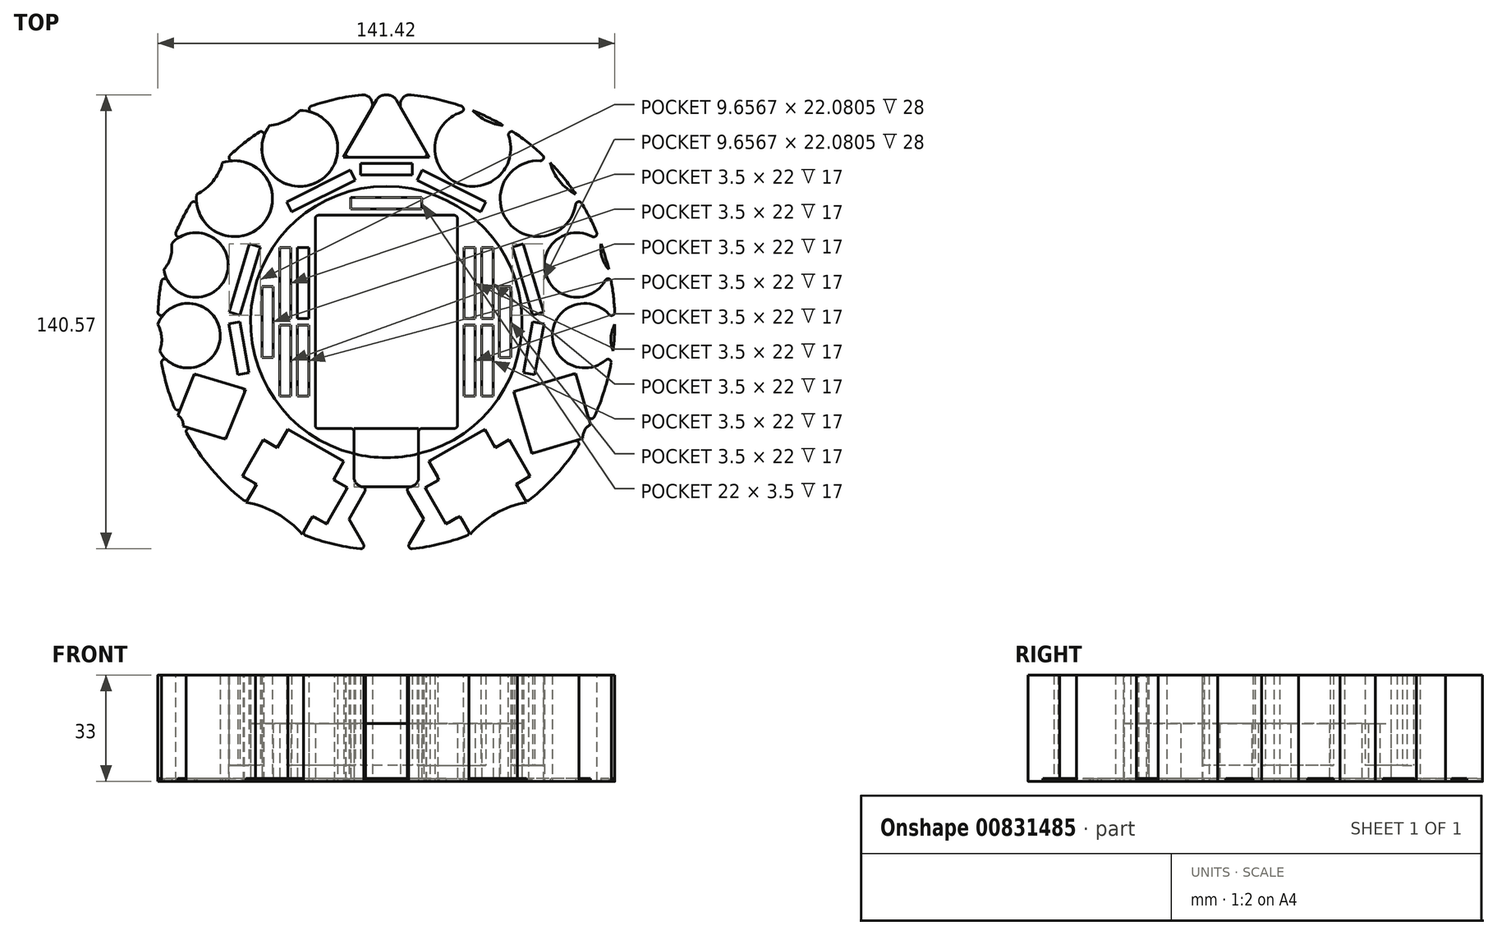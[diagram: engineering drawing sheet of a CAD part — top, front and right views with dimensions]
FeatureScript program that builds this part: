
annotation { "Feature Type Name" : "Feature", "Feature Type Description" : "" }
export const myFeature = defineFeature(function(context is Context, id is Id, definition is map)
    precondition{}
    {
        {
            var Q0;
            Q0=qCreatedBy(makeId("Top.planeOp"),FACE);
            var sketch = newSketch(context, id + "F0", { "sketchPlane" : qUnion([Q0])});
            skLineSegment(sketch, "E0.bottom", {"start": v(-22, 33) * mm, "end": v(22, 33) * mm});
            skLineSegment(sketch, "E0.top", {"start": v(-22, -33) * mm, "end": v(22, -33) * mm});
            skLineSegment(sketch, "E0.left", {"start": v(-22, 33) * mm, "end": v(-22, -33) * mm});
            skLineSegment(sketch, "E0.right", {"start": v(22, 33) * mm, "end": v(22, -33) * mm});
            skPoint(sketch, "E0.middle", {"position": v(0, 0) * mm});
            skCircle(sketch, "E1", {"center": v(0, 0) * mm, "radius": 42 * mm});
            skCircle(sketch, "E2", {"center": v(0, 0) * mm, "radius": 70.71 * mm});
            skPoint(sketch, "E3.middle", {"position": v(0, 57) * mm});
            skLineSegment(sketch, "E4.bottom", {"start": v(-10, -33) * mm, "end": v(10, -33) * mm});
            skLineSegment(sketch, "E4.top", {"start": v(-10, -51) * mm, "end": v(10, -51) * mm});
            skLineSegment(sketch, "E4.left", {"start": v(-10, -33) * mm, "end": v(-10, -51) * mm});
            skLineSegment(sketch, "E4.right", {"start": v(10, -33) * mm, "end": v(10, -51) * mm});
            skPoint(sketch, "E4.middle", {"position": v(0, -42) * mm});
            skCircle(sketch, "E5", {"center": v(0, 0) * mm, "radius": 60 * mm, "construction": true});
            skCircle(sketch, "E6", {"center": v(26.76, 53.7) * mm, "radius": 11.75 * mm});
            skCircle(sketch, "E7", {"center": v(0, 0) * mm, "radius": 61.5 * mm, "construction": true});
            skCircle(sketch, "E8", {"center": v(58.92, 17.62) * mm, "radius": 10 * mm});
            skCircle(sketch, "E9", {"center": v(0, 0) * mm, "radius": 60.5 * mm, "construction": true});
            skCircle(sketch, "E10", {"center": v(46.96, 38.14) * mm, "radius": 11.75 * mm});
            skCircle(sketch, "E11", {"center": v(61.35, -4.24) * mm, "radius": 10 * mm});
            skLineSegment(sketch, "E12", {"start": v(-13.28, 51) * mm, "end": v(13.28, 51) * mm});
            skLineSegment(sketch, "E13", {"start": v(13.28, 51) * mm, "end": v(0, 74) * mm});
            skLineSegment(sketch, "E14", {"start": v(0, 74) * mm, "end": v(-13.28, 51) * mm});
            skCircle(sketch, "E15", {"center": v(0, 0) * mm, "radius": 74 * mm, "construction": true});
            skCircle(sketch, "E16", {"center": v(0, 0) * mm, "radius": 59 * mm, "construction": true});
            skLineSegment(sketch, "E17", {"start": v(0, 0) * mm, "end": v(51.76, -28.32) * mm, "construction": true});
            skLineSegment(sketch, "E18.bottom", {"start": v(64.17, -35.1) * mm, "end": v(44.97, -40.72) * mm});
            skLineSegment(sketch, "E18.top", {"start": v(58.55, -15.91) * mm, "end": v(39.35, -21.53) * mm});
            skLineSegment(sketch, "E18.left", {"start": v(64.17, -35.1) * mm, "end": v(58.55, -15.91) * mm});
            skLineSegment(sketch, "E18.right", {"start": v(44.97, -40.72) * mm, "end": v(39.35, -21.53) * mm});
            skPoint(sketch, "E18.middle", {"position": v(51.76, -28.32) * mm});
            skCircle(sketch, "E19.MirrorC", {"center": v(-26.76, 53.7) * mm, "radius": 11.75 * mm});
            skCircle(sketch, "E20.MirrorC", {"center": v(-46.96, 38.14) * mm, "radius": 11.75 * mm});
            skCircle(sketch, "E21.MirrorC", {"center": v(-58.92, 17.62) * mm, "radius": 10 * mm});
            skCircle(sketch, "E22.MirrorC", {"center": v(-61.35, -4.24) * mm, "radius": 10 * mm});
            skLineSegment(sketch, "E23", {"start": v(-65.56, -31.45) * mm, "end": v(-49.7, -36.26) * mm});
            skLineSegment(sketch, "E24", {"start": v(-49.7, -36.26) * mm, "end": v(-43.54, -20.89) * mm});
            skLineSegment(sketch, "E25", {"start": v(-43.54, -20.89) * mm, "end": v(-59.39, -16.08) * mm});
            skLineSegment(sketch, "E26", {"start": v(-59.39, -16.08) * mm, "end": v(-65.56, -31.45) * mm});
            skLineSegment(sketch, "E27.bottom", {"start": v(-18.44, -62.59) * mm, "end": v(-44.5, -47.72) * mm});
            skLineSegment(sketch, "E27.top", {"start": v(-12, -51.3) * mm, "end": v(-38.06, -36.43) * mm});
            skLineSegment(sketch, "E27.left", {"start": v(-18.44, -62.59) * mm, "end": v(-12, -51.3) * mm});
            skLineSegment(sketch, "E27.right", {"start": v(-44.5, -47.72) * mm, "end": v(-38.06, -36.43) * mm});
            skPoint(sketch, "E27.middle", {"position": v(-28.25, -49.5) * mm});
            skLineSegment(sketch, "E28.bottom", {"start": v(-13.12, -43.17) * mm, "end": v(-30.5, -33.26) * mm});
            skLineSegment(sketch, "E28.top", {"start": v(-26, -65.75) * mm, "end": v(-43.38, -55.84) * mm});
            skLineSegment(sketch, "E28.left", {"start": v(-13.12, -43.17) * mm, "end": v(-26, -65.75) * mm});
            skLineSegment(sketch, "E28.right", {"start": v(-30.5, -33.26) * mm, "end": v(-43.38, -55.84) * mm});
            skLineSegment(sketch, "E29", {"start": v(0, 0) * mm, "end": v(-116.4, -55.84) * mm, "construction": true});
            skLineSegment(sketch, "E30.MirrorCS", {"start": v(13.12, -43.17) * mm, "end": v(30.5, -33.26) * mm});
            skLineSegment(sketch, "E31.MirrorCS", {"start": v(12, -51.3) * mm, "end": v(38.06, -36.43) * mm});
            skLineSegment(sketch, "E32.MirrorCS", {"start": v(30.5, -33.26) * mm, "end": v(43.38, -55.84) * mm});
            skLineSegment(sketch, "E33.MirrorCS", {"start": v(44.5, -47.72) * mm, "end": v(38.06, -36.43) * mm});
            skLineSegment(sketch, "E34.MirrorCS", {"start": v(18.44, -62.59) * mm, "end": v(12, -51.3) * mm});
            skLineSegment(sketch, "E35.MirrorCS", {"start": v(13.12, -43.17) * mm, "end": v(26, -65.75) * mm});
            skLineSegment(sketch, "E36.MirrorCS", {"start": v(26, -65.75) * mm, "end": v(43.38, -55.84) * mm});
            skLineSegment(sketch, "E37.MirrorCS", {"start": v(18.44, -62.59) * mm, "end": v(44.5, -47.72) * mm});
            skLineSegment(sketch, "E38", {"start": v(-24, 29.08) * mm, "end": v(-24, -29.92) * mm, "construction": true});
            skCircle(sketch, "E39", {"center": v(0, 0) * mm, "radius": 40 * mm, "construction": true});
            skLineSegment(sketch, "E40", {"start": v(-46.76, 1) * mm, "end": v(-10.29, 1) * mm, "construction": true});
            skLineSegment(sketch, "E41.bottom", {"start": v(-24, 1) * mm, "end": v(-27.5, 1) * mm});
            skLineSegment(sketch, "E41.top", {"start": v(-24, 23) * mm, "end": v(-27.5, 23) * mm});
            skLineSegment(sketch, "E41.left", {"start": v(-24, 1) * mm, "end": v(-24, 23) * mm});
            skLineSegment(sketch, "E41.right", {"start": v(-27.5, 1) * mm, "end": v(-27.5, 23) * mm});
            skLineSegment(sketch, "E42.bottom", {"start": v(-29.5, 1) * mm, "end": v(-33, 1) * mm});
            skLineSegment(sketch, "E42.top", {"start": v(-29.5, 23) * mm, "end": v(-33, 23) * mm});
            skLineSegment(sketch, "E42.left", {"start": v(-29.5, 1) * mm, "end": v(-29.5, 23) * mm});
            skLineSegment(sketch, "E42.right", {"start": v(-33, 1) * mm, "end": v(-33, 23) * mm});
            skLineSegment(sketch, "E43.bottom", {"start": v(-35, 11) * mm, "end": v(-38.5, 11) * mm});
            skLineSegment(sketch, "E43.top", {"start": v(-35, -11) * mm, "end": v(-38.5, -11) * mm});
            skLineSegment(sketch, "E43.left", {"start": v(-35, 11) * mm, "end": v(-35, -11) * mm});
            skLineSegment(sketch, "E43.right", {"start": v(-38.5, 11) * mm, "end": v(-38.5, -11) * mm});
            skPoint(sketch, "E43.middle", {"position": v(-36.75, 0) * mm});
            skLineSegment(sketch, "E44.MirrorCS", {"start": v(-29.5, -1) * mm, "end": v(-29.5, -23) * mm});
            skLineSegment(sketch, "E45.MirrorCS", {"start": v(-27.5, -1) * mm, "end": v(-27.5, -23) * mm});
            skLineSegment(sketch, "E46.MirrorCS", {"start": v(-29.5, -1) * mm, "end": v(-33, -1) * mm});
            skLineSegment(sketch, "E47.MirrorCS", {"start": v(-24, -1) * mm, "end": v(-27.5, -1) * mm});
            skLineSegment(sketch, "E48.MirrorCS", {"start": v(-24, -23) * mm, "end": v(-27.5, -23) * mm});
            skLineSegment(sketch, "E49.MirrorCS", {"start": v(-29.5, -23) * mm, "end": v(-33, -23) * mm});
            skLineSegment(sketch, "E50.MirrorCS", {"start": v(-33, -1) * mm, "end": v(-33, -23) * mm});
            skLineSegment(sketch, "E51.MirrorCS", {"start": v(-24, -1) * mm, "end": v(-24, -23) * mm});
            skLineSegment(sketch, "E52.MirrorCS", {"start": v(24, -1) * mm, "end": v(24, -23) * mm});
            skLineSegment(sketch, "E53.MirrorCS", {"start": v(24, 1) * mm, "end": v(24, 23) * mm});
            skLineSegment(sketch, "E54.MirrorCS", {"start": v(29.5, 1) * mm, "end": v(33, 1) * mm});
            skLineSegment(sketch, "E55.MirrorCS", {"start": v(29.5, -1) * mm, "end": v(33, -1) * mm});
            skLineSegment(sketch, "E56.MirrorCS", {"start": v(24, 1) * mm, "end": v(27.5, 1) * mm});
            skLineSegment(sketch, "E57.MirrorCS", {"start": v(24, -1) * mm, "end": v(27.5, -1) * mm});
            skLineSegment(sketch, "E58.MirrorCS", {"start": v(24, 29.08) * mm, "end": v(24, -29.92) * mm, "construction": true});
            skLineSegment(sketch, "E59.MirrorCS", {"start": v(24, -23) * mm, "end": v(27.5, -23) * mm});
            skLineSegment(sketch, "E60.MirrorCS", {"start": v(35, 11) * mm, "end": v(38.5, 11) * mm});
            skLineSegment(sketch, "E61.MirrorCS", {"start": v(29.5, -1) * mm, "end": v(29.5, -23) * mm});
            skLineSegment(sketch, "E62.MirrorCS", {"start": v(35, -11) * mm, "end": v(38.5, -11) * mm});
            skLineSegment(sketch, "E63.MirrorCS", {"start": v(29.5, 23) * mm, "end": v(33, 23) * mm});
            skLineSegment(sketch, "E64.MirrorCS", {"start": v(38.5, 11) * mm, "end": v(38.5, -11) * mm});
            skLineSegment(sketch, "E65.MirrorCS", {"start": v(24, 23) * mm, "end": v(27.5, 23) * mm});
            skPoint(sketch, "E66.MirrorP", {"position": v(36.75, 0) * mm});
            skLineSegment(sketch, "E67.MirrorCS", {"start": v(46.76, 1) * mm, "end": v(10.29, 1) * mm, "construction": true});
            skLineSegment(sketch, "E68.MirrorCS", {"start": v(27.5, -1) * mm, "end": v(27.5, -23) * mm});
            skLineSegment(sketch, "E69.MirrorCS", {"start": v(33, 1) * mm, "end": v(33, 23) * mm});
            skLineSegment(sketch, "E70.MirrorCS", {"start": v(35, 11) * mm, "end": v(35, -11) * mm});
            skLineSegment(sketch, "E71.MirrorCS", {"start": v(29.5, -23) * mm, "end": v(33, -23) * mm});
            skLineSegment(sketch, "E72.MirrorCS", {"start": v(29.5, 1) * mm, "end": v(29.5, 23) * mm});
            skLineSegment(sketch, "E73.MirrorCS", {"start": v(27.5, 1) * mm, "end": v(27.5, 23) * mm});
            skLineSegment(sketch, "E74.MirrorCS", {"start": v(33, -1) * mm, "end": v(33, -23) * mm});
            skLineSegment(sketch, "E75.bottom", {"start": v(11, 35) * mm, "end": v(-11, 35) * mm});
            skLineSegment(sketch, "E75.top", {"start": v(11, 38.5) * mm, "end": v(-11, 38.5) * mm});
            skLineSegment(sketch, "E75.left", {"start": v(11, 35) * mm, "end": v(11, 38.5) * mm});
            skLineSegment(sketch, "E75.right", {"start": v(-11, 35) * mm, "end": v(-11, 38.5) * mm});
            skPoint(sketch, "E75.middle", {"position": v(0, 36.75) * mm});
            skLineSegment(sketch, "E76", {"start": v(0, 0) * mm, "end": v(-26.76, 53.7) * mm, "construction": true});
            skLineSegment(sketch, "E77.bottom", {"start": v(-11.12, 46.97) * mm, "end": v(-30.8, 37.16) * mm});
            skLineSegment(sketch, "E77.top", {"start": v(-9.56, 43.84) * mm, "end": v(-29.25, 34.03) * mm});
            skLineSegment(sketch, "E77.left", {"start": v(-11.12, 46.97) * mm, "end": v(-9.56, 43.84) * mm});
            skLineSegment(sketch, "E77.right", {"start": v(-30.8, 37.16) * mm, "end": v(-29.25, 34.03) * mm});
            skPoint(sketch, "E77.middle", {"position": v(-20.18, 40.5) * mm});
            skLineSegment(sketch, "E78", {"start": v(-58.92, 17.62) * mm, "end": v(0, 0) * mm, "construction": true});
            skLineSegment(sketch, "E79.bottom", {"start": v(-39, 23.15) * mm, "end": v(-42.36, 24.15) * mm});
            skLineSegment(sketch, "E79.top", {"start": v(-45.3, 2.07) * mm, "end": v(-48.66, 3.07) * mm});
            skLineSegment(sketch, "E79.left", {"start": v(-39, 23.15) * mm, "end": v(-45.3, 2.07) * mm});
            skLineSegment(sketch, "E79.right", {"start": v(-42.36, 24.15) * mm, "end": v(-48.66, 3.07) * mm});
            skPoint(sketch, "E79.middle", {"position": v(-43.83, 13.1) * mm});
            skLineSegment(sketch, "E80.MirrorCS", {"start": v(30.8, 37.16) * mm, "end": v(29.25, 34.03) * mm});
            skLineSegment(sketch, "E81.MirrorCS", {"start": v(11.12, 46.97) * mm, "end": v(30.8, 37.16) * mm});
            skLineSegment(sketch, "E82.MirrorCS", {"start": v(9.56, 43.84) * mm, "end": v(29.25, 34.03) * mm});
            skLineSegment(sketch, "E83.MirrorCS", {"start": v(11.12, 46.97) * mm, "end": v(9.56, 43.84) * mm});
            skLineSegment(sketch, "E84.MirrorCS", {"start": v(42.36, 24.15) * mm, "end": v(48.66, 3.07) * mm});
            skLineSegment(sketch, "E85.MirrorCS", {"start": v(39, 23.15) * mm, "end": v(45.3, 2.07) * mm});
            skLineSegment(sketch, "E86.MirrorCS", {"start": v(39, 23.15) * mm, "end": v(42.36, 24.15) * mm});
            skLineSegment(sketch, "E87.MirrorCS", {"start": v(45.3, 2.07) * mm, "end": v(48.66, 3.07) * mm});
            skLineSegment(sketch, "E88.bottom", {"start": v(8, 45.5) * mm, "end": v(-8, 45.5) * mm});
            skLineSegment(sketch, "E88.top", {"start": v(8, 49) * mm, "end": v(-8, 49) * mm});
            skLineSegment(sketch, "E88.left", {"start": v(8, 45.5) * mm, "end": v(8, 49) * mm});
            skLineSegment(sketch, "E88.right", {"start": v(-8, 45.5) * mm, "end": v(-8, 49) * mm});
            skPoint(sketch, "E88.middle", {"position": v(0, 47.25) * mm});
            skLineSegment(sketch, "E89", {"start": v(0, 0) * mm, "end": v(-52.56, -9.43) * mm, "construction": true});
            skLineSegment(sketch, "E90.bottom", {"start": v(-48.75, -0.62) * mm, "end": v(-45.3, 0) * mm});
            skLineSegment(sketch, "E90.top", {"start": v(-45.93, -16.37) * mm, "end": v(-42.48, -15.75) * mm});
            skLineSegment(sketch, "E90.left", {"start": v(-48.75, -0.62) * mm, "end": v(-45.93, -16.37) * mm});
            skLineSegment(sketch, "E90.right", {"start": v(-45.3, 0) * mm, "end": v(-42.48, -15.75) * mm});
            skPoint(sketch, "E90.middle", {"position": v(-45.62, -8.18) * mm});
            skLineSegment(sketch, "E91.MirrorCS", {"start": v(48.75, -0.62) * mm, "end": v(45.3, 0) * mm});
            skLineSegment(sketch, "E92.MirrorCS", {"start": v(45.93, -16.37) * mm, "end": v(42.48, -15.75) * mm});
            skLineSegment(sketch, "E93.MirrorCS", {"start": v(48.75, -0.62) * mm, "end": v(45.93, -16.37) * mm});
            skLineSegment(sketch, "E94.MirrorCS", {"start": v(45.3, 0) * mm, "end": v(42.48, -15.75) * mm});
            skPoint(sketch, "E95.MirrorP", {"position": v(45.62, -8.18) * mm});
            skLineSegment(sketch, "E96", {"start": v(-45.3, 2.07) * mm, "end": v(-45.3, -7.96) * mm, "construction": true});
            skCircle(sketch, "E97.cCircle", {"center": v(0, -61) * mm, "radius": 10 * mm, "construction": true});
            skLineSegment(sketch, "E97.0", {"start": v(-5.77, -51) * mm, "end": v(5.77, -51) * mm});
            skLineSegment(sketch, "E97.1", {"start": v(5.77, -51) * mm, "end": v(11.55, -61) * mm});
            skLineSegment(sketch, "E97.2", {"start": v(11.55, -61) * mm, "end": v(5.77, -71) * mm});
            skLineSegment(sketch, "E97.3", {"start": v(5.77, -71) * mm, "end": v(-5.77, -71) * mm});
            skLineSegment(sketch, "E97.4", {"start": v(-5.77, -71) * mm, "end": v(-11.55, -61) * mm});
            skLineSegment(sketch, "E97.5", {"start": v(-11.55, -61) * mm, "end": v(-5.77, -51) * mm});
            skPoint(sketch, "E97.0.midPoint", {"position": v(0, -51) * mm});
            skArc(sketch, "E98", {"start": v(-26, -65.75) * mm, "mid": v(-33.84, -59.3) * mm, "end": v(-43.38, -55.84) * mm});
            skArc(sketch, "E99", {"start": v(43.38, -55.84) * mm, "mid": v(33.84, -59.3) * mm, "end": v(26, -65.75) * mm});
            skArc(sketch, "E100", {"start": v(6.1, -70.45) * mm, "mid": v(0, -69.82) * mm, "end": v(-6.1, -70.45) * mm});
            skArc(sketch, "E101", {"start": v(-62.93, -32.25) * mm, "mid": v(-63.18, -30.31) * mm, "end": v(-64.53, -28.9) * mm});
            skArc(sketch, "E102", {"start": v(-70.13, -9.03) * mm, "mid": v(-69.5, -4.8) * mm, "end": v(-70.7, -0.7) * mm});
            skArc(sketch, "E103", {"start": v(-68.82, 16.23) * mm, "mid": v(-66.75, 19.96) * mm, "end": v(-66.43, 24.22) * mm});
            skArc(sketch, "E104", {"start": v(-58.63, 39.53) * mm, "mid": v(-53.6, 43.53) * mm, "end": v(-50.71, 49.28) * mm});
            skArc(sketch, "E105", {"start": v(-36.14, 60.78) * mm, "mid": v(-31.03, 62.27) * mm, "end": v(-26.76, 65.45) * mm});
            skArc(sketch, "E106", {"start": v(-1.91, 70.68) * mm, "mid": v(0, 70.2) * mm, "end": v(1.91, 70.68) * mm});
            skArc(sketch, "E107", {"start": v(63.18, -31.75) * mm, "mid": v(61.34, -33.56) * mm, "end": v(60.8, -36.09) * mm});
            skArc(sketch, "E108.MirrorCS", {"start": v(36.14, 60.78) * mm, "mid": v(31.03, 62.27) * mm, "end": v(26.76, 65.45) * mm});
            skArc(sketch, "E109.MirrorCS", {"start": v(58.63, 39.53) * mm, "mid": v(53.6, 43.53) * mm, "end": v(50.71, 49.28) * mm});
            skArc(sketch, "E110.MirrorCS", {"start": v(68.82, 16.23) * mm, "mid": v(66.75, 19.96) * mm, "end": v(66.43, 24.22) * mm});
            skArc(sketch, "E111.MirrorCS", {"start": v(70.13, -9.03) * mm, "mid": v(69.5, -4.8) * mm, "end": v(70.7, -0.7) * mm});
            skSolve(sketch);
        }
        {
            var Q0;
            Q0=makeQuery(id+"F0.imprint","IMPRINT",FACE,{"disambiguationData":[TD([[makeQuery(id+"F0.imprint","IMPRINT",EDGE,{"derivedFrom":sQuery(id+"F0.wireOp",EDGE,"E0.bottom")}),1.0]])]});
            extrude(context, id + "F1", {"entities" : qUnion([Q0]), "depth" : 18 * mm, "offsetDistance" : 25 * mm});
        }
        {
            var Q0;
            {var subQ0=sQuery(id+"F0.wireOp",EDGE,"E3.bottom");Q0=makeQuery(id+"F0.imprint","IMPRINT",FACE,{"disambiguationData":[TD([[makeQuery(id+"F0.imprint","IMPRINT",EDGE,{"derivedFrom":subQ0}),-1.0]])]});}
            var Q1;
            {var subQ0=sQuery(id+"F0.wireOp",EDGE,"wK9GQTOU-0l9T-mlqG-xWPM-1yL7ZsGGjNM9.top");var subQ1=sQuery(id+"F0.wireOp",EDGE,"E3.left");var subQ2=makeQuery(id+"F0.imprint","INTERSECT",VERTEX,{"derivedFrom":[subQ1,subQ0]});Q1=makeQuery(id+"F0.imprint","IMPRINT",FACE,{"disambiguationData":[TD([[makeQuery(id+"F0.imprint","IMPRINT",EDGE,{"disambiguationData":[TD([[subQ2,-1.0]])],"derivedFrom":subQ1}),1.0]])]});}
            var Q2;
            {var subQ5=sQuery(id+"F0.wireOp",EDGE,"wK9GQTOU-0l9T-mlqG-xWPM-1yL7ZsGGjNM9.right");Q2=makeQuery(id+"F0.imprint","IMPRINT",FACE,{"disambiguationData":[TD([[makeQuery(id+"F0.imprint","IMPRINT",EDGE,{"derivedFrom":subQ5}),-1.0]])]});}
            var Q3;
            {var subQ5=sQuery(id+"F0.wireOp",EDGE,"wK9GQTOU-0l9T-mlqG-xWPM-1yL7ZsGGjNM9.left");Q3=makeQuery(id+"F0.imprint","IMPRINT",FACE,{"disambiguationData":[TD([[makeQuery(id+"F0.imprint","IMPRINT",EDGE,{"derivedFrom":subQ5}),1.0]])]});}
            var Q4;
            {var subQ0=sQuery(id+"F0.wireOp",EDGE,"E3.top");Q4=makeQuery(id+"F0.imprint","IMPRINT",FACE,{"disambiguationData":[TD([[makeQuery(id+"F0.imprint","IMPRINT",EDGE,{"derivedFrom":subQ0}),1.0]])]});}
            var Q5;
            {var subQ0=sQuery(id+"F0.wireOp",EDGE,"E3.bottom");Q5=makeQuery(id+"F0.imprint","IMPRINT",FACE,{"disambiguationData":[TD([[makeQuery(id+"F0.imprint","IMPRINT",EDGE,{"derivedFrom":subQ0}),1.0]])]});}
            var Q6;
            Q6=makeQuery(id+"F0.imprint","IMPRINT",FACE,{"disambiguationData":[TD([[makeQuery(id+"F0.imprint","IMPRINT",EDGE,{"derivedFrom":sQuery(id+"F0.wireOp",EDGE,"E0.bottom")}),-1.0]])]});
            var Q7;
            {var subQ5=sQuery(id+"F0.wireOp",EDGE,"E4.top");Q7=makeQuery(id+"F0.imprint","IMPRINT",FACE,{"disambiguationData":[TD([[makeQuery(id+"F0.imprint","IMPRINT",EDGE,{"derivedFrom":subQ5}),1.0]])]});}
            var Q8;
            {var subQ5=sQuery(id+"F0.wireOp",EDGE,"E4.bottom");Q8=makeQuery(id+"F0.imprint","IMPRINT",FACE,{"disambiguationData":[TD([[makeQuery(id+"F0.imprint","IMPRINT",EDGE,{"derivedFrom":subQ5}),-1.0]])]});}
            var Q9;
            {var subQ0=sQuery(id+"F0.wireOp",EDGE,"382944a8-2fda-4f8f-b6c7-34ecd0944c6e0.MirrorCS");Q9=makeQuery(id+"F0.imprint","IMPRINT",FACE,{"disambiguationData":[TD([[makeQuery(id+"F0.imprint","IMPRINT",EDGE,{"derivedFrom":subQ0}),-1.0]])]});}
            var Q10;
            {var subQ0=sQuery(id+"F0.wireOp",EDGE,"E18.top");Q10=makeQuery(id+"F0.imprint","IMPRINT",FACE,{"disambiguationData":[TD([[makeQuery(id+"F0.imprint","IMPRINT",EDGE,{"derivedFrom":subQ0}),1.0]])]});}
            var Q11;
            {var subQ1=sQuery(id+"F0.wireOp",EDGE,"E24");Q11=makeQuery(id+"F0.imprint","IMPRINT",FACE,{"disambiguationData":[TD([[makeQuery(id+"F0.imprint","IMPRINT",EDGE,{"derivedFrom":subQ1}),1.0]])]});}
            var Q12;
            {var subQ5=sQuery(id+"F0.wireOp",EDGE,"E12");Q12=makeQuery(id+"F0.imprint","IMPRINT",FACE,{"disambiguationData":[TD([[makeQuery(id+"F0.imprint","IMPRINT",EDGE,{"derivedFrom":subQ5}),1.0]])]});}
            var Q13;
            {var subQ5=sQuery(id+"F0.wireOp",EDGE,"E28.bottom");Q13=makeQuery(id+"F0.imprint","IMPRINT",FACE,{"disambiguationData":[TD([[makeQuery(id+"F0.imprint","IMPRINT",EDGE,{"derivedFrom":subQ5}),1.0]])]});}
            var Q14;
            {var subQ0=sQuery(id+"F0.wireOp",EDGE,"E27.right");Q14=makeQuery(id+"F0.imprint","IMPRINT",FACE,{"disambiguationData":[TD([[makeQuery(id+"F0.imprint","IMPRINT",EDGE,{"derivedFrom":subQ0}),-1.0]])]});}
            var Q15;
            {var subQ0=sQuery(id+"F0.wireOp",EDGE,"E28.left");var subQ1=sQuery(id+"F0.wireOp",EDGE,"E27.bottom");var subQ2=makeQuery(id+"F0.imprint","INTERSECT",VERTEX,{"derivedFrom":[subQ1,subQ0]});Q15=makeQuery(id+"F0.imprint","IMPRINT",FACE,{"disambiguationData":[TD([[makeQuery(id+"F0.imprint","IMPRINT",EDGE,{"disambiguationData":[TD([[subQ2,-1.0]])],"derivedFrom":subQ1}),-1.0]])]});}
            var Q16;
            {var subQ0=sQuery(id+"F0.wireOp",EDGE,"E27.left");Q16=makeQuery(id+"F0.imprint","IMPRINT",FACE,{"disambiguationData":[TD([[makeQuery(id+"F0.imprint","IMPRINT",EDGE,{"derivedFrom":subQ0}),1.0]])]});}
            var Q17;
            {var subQ0=sQuery(id+"F0.wireOp",EDGE,"E30.MirrorCS");Q17=makeQuery(id+"F0.imprint","IMPRINT",FACE,{"disambiguationData":[TD([[makeQuery(id+"F0.imprint","IMPRINT",EDGE,{"derivedFrom":subQ0}),-1.0]])]});}
            var Q18;
            {var subQ0=sQuery(id+"F0.wireOp",EDGE,"E35.MirrorCS");var subQ1=sQuery(id+"F0.wireOp",EDGE,"E31.MirrorCS");var subQ2=makeQuery(id+"F0.imprint","INTERSECT",VERTEX,{"derivedFrom":[subQ1,subQ0]});Q18=makeQuery(id+"F0.imprint","IMPRINT",FACE,{"disambiguationData":[TD([[makeQuery(id+"F0.imprint","IMPRINT",EDGE,{"disambiguationData":[TD([[subQ2,-1.0]])],"derivedFrom":subQ1}),-1.0]])]});}
            var Q19;
            {var subQ0=sQuery(id+"F0.wireOp",EDGE,"E34.MirrorCS");Q19=makeQuery(id+"F0.imprint","IMPRINT",FACE,{"disambiguationData":[TD([[makeQuery(id+"F0.imprint","IMPRINT",EDGE,{"derivedFrom":subQ0}),-1.0]])]});}
            var Q20;
            {var subQ0=sQuery(id+"F0.wireOp",EDGE,"E33.MirrorCS");Q20=makeQuery(id+"F0.imprint","IMPRINT",FACE,{"disambiguationData":[TD([[makeQuery(id+"F0.imprint","IMPRINT",EDGE,{"derivedFrom":subQ0}),1.0]])]});}
            var Q21;
            Q21=makeQuery(id+"F0.imprint","IMPRINT",FACE,{"disambiguationData":[TD([[makeQuery(id+"F0.imprint","IMPRINT",EDGE,{"derivedFrom":sQuery(id+"F0.wireOp",EDGE,"E43.bottom")}),1.0]])]});
            var Q22;
            Q22=makeQuery(id+"F0.imprint","IMPRINT",FACE,{"disambiguationData":[TD([[makeQuery(id+"F0.imprint","IMPRINT",EDGE,{"derivedFrom":sQuery(id+"F0.wireOp",EDGE,"E42.bottom")}),-1.0]])]});
            var Q23;
            Q23=makeQuery(id+"F0.imprint","IMPRINT",FACE,{"disambiguationData":[TD([[makeQuery(id+"F0.imprint","IMPRINT",EDGE,{"derivedFrom":sQuery(id+"F0.wireOp",EDGE,"E41.bottom")}),-1.0]])]});
            var Q24;
            Q24=makeQuery(id+"F0.imprint","IMPRINT",FACE,{"disambiguationData":[TD([[makeQuery(id+"F0.imprint","IMPRINT",EDGE,{"derivedFrom":sQuery(id+"F0.wireOp",EDGE,"E44.MirrorCS")}),-1.0]])]});
            var Q25;
            Q25=makeQuery(id+"F0.imprint","IMPRINT",FACE,{"disambiguationData":[TD([[makeQuery(id+"F0.imprint","IMPRINT",EDGE,{"derivedFrom":sQuery(id+"F0.wireOp",EDGE,"E53.MirrorCS")}),-1.0]])]});
            var Q26;
            Q26=makeQuery(id+"F0.imprint","IMPRINT",FACE,{"disambiguationData":[TD([[makeQuery(id+"F0.imprint","IMPRINT",EDGE,{"derivedFrom":sQuery(id+"F0.wireOp",EDGE,"E54.MirrorCS")}),1.0]])]});
            var Q27;
            Q27=makeQuery(id+"F0.imprint","IMPRINT",FACE,{"disambiguationData":[TD([[makeQuery(id+"F0.imprint","IMPRINT",EDGE,{"derivedFrom":sQuery(id+"F0.wireOp",EDGE,"E60.MirrorCS")}),-1.0]])]});
            var Q28;
            Q28=makeQuery(id+"F0.imprint","IMPRINT",FACE,{"disambiguationData":[TD([[makeQuery(id+"F0.imprint","IMPRINT",EDGE,{"derivedFrom":sQuery(id+"F0.wireOp",EDGE,"E55.MirrorCS")}),-1.0]])]});
            var Q29;
            Q29=makeQuery(id+"F0.imprint","IMPRINT",FACE,{"disambiguationData":[TD([[makeQuery(id+"F0.imprint","IMPRINT",EDGE,{"derivedFrom":sQuery(id+"F0.wireOp",EDGE,"E52.MirrorCS")}),1.0]])]});
            var Q30;
            Q30=makeQuery(id+"F0.imprint","IMPRINT",FACE,{"disambiguationData":[TD([[makeQuery(id+"F0.imprint","IMPRINT",EDGE,{"derivedFrom":sQuery(id+"F0.wireOp",EDGE,"E45.MirrorCS")}),1.0]])]});
            var Q31;
            Q31=makeQuery(id+"F0.imprint","IMPRINT",FACE,{"disambiguationData":[TD([[makeQuery(id+"F0.imprint","IMPRINT",EDGE,{"derivedFrom":sQuery(id+"F0.wireOp",EDGE,"E75.bottom")}),-1.0]])]});
            var Q32;
            Q32=makeQuery(id+"F0.imprint","IMPRINT",FACE,{"disambiguationData":[TD([[makeQuery(id+"F0.imprint","IMPRINT",EDGE,{"derivedFrom":sQuery(id+"F0.wireOp",EDGE,"E97.0")}),-1.0]])]});
            var Q33;
            {var subQ5=sQuery(id+"F0.wireOp",EDGE,"E98");Q33=makeQuery(id+"F0.imprint","IMPRINT",FACE,{"disambiguationData":[TD([[makeQuery(id+"F0.imprint","IMPRINT",EDGE,{"derivedFrom":subQ5}),-1.0]])]});}
            var Q34;
            {var subQ0=sQuery(id+"F0.wireOp",EDGE,"E99");Q34=makeQuery(id+"F0.imprint","IMPRINT",FACE,{"disambiguationData":[TD([[makeQuery(id+"F0.imprint","IMPRINT",EDGE,{"derivedFrom":subQ0}),-1.0]])]});}
            var Q35;
            {var subQ0=sQuery(id+"F0.wireOp",EDGE,"E102");Q35=makeQuery(id+"F0.imprint","IMPRINT",FACE,{"disambiguationData":[TD([[makeQuery(id+"F0.imprint","IMPRINT",EDGE,{"derivedFrom":subQ0}),-1.0]])]});}
            var Q36;
            {var subQ0=sQuery(id+"F0.wireOp",EDGE,"E103");Q36=makeQuery(id+"F0.imprint","IMPRINT",FACE,{"disambiguationData":[TD([[makeQuery(id+"F0.imprint","IMPRINT",EDGE,{"derivedFrom":subQ0}),-1.0]])]});}
            var Q37;
            {var subQ0=sQuery(id+"F0.wireOp",EDGE,"E104");Q37=makeQuery(id+"F0.imprint","IMPRINT",FACE,{"disambiguationData":[TD([[makeQuery(id+"F0.imprint","IMPRINT",EDGE,{"derivedFrom":subQ0}),-1.0]])]});}
            var Q38;
            {var subQ0=sQuery(id+"F0.wireOp",EDGE,"E105");Q38=makeQuery(id+"F0.imprint","IMPRINT",FACE,{"disambiguationData":[TD([[makeQuery(id+"F0.imprint","IMPRINT",EDGE,{"derivedFrom":subQ0}),-1.0]])]});}
            var Q39;
            {var subQ0=sQuery(id+"F0.wireOp",EDGE,"E108.MirrorCS");Q39=makeQuery(id+"F0.imprint","IMPRINT",FACE,{"disambiguationData":[TD([[makeQuery(id+"F0.imprint","IMPRINT",EDGE,{"derivedFrom":subQ0}),1.0]])]});}
            var Q40;
            {var subQ0=sQuery(id+"F0.wireOp",EDGE,"E109.MirrorCS");Q40=makeQuery(id+"F0.imprint","IMPRINT",FACE,{"disambiguationData":[TD([[makeQuery(id+"F0.imprint","IMPRINT",EDGE,{"derivedFrom":subQ0}),1.0]])]});}
            var Q41;
            {var subQ0=sQuery(id+"F0.wireOp",EDGE,"E110.MirrorCS");Q41=makeQuery(id+"F0.imprint","IMPRINT",FACE,{"disambiguationData":[TD([[makeQuery(id+"F0.imprint","IMPRINT",EDGE,{"derivedFrom":subQ0}),1.0]])]});}
            var Q42;
            {var subQ0=sQuery(id+"F0.wireOp",EDGE,"E111.MirrorCS");Q42=makeQuery(id+"F0.imprint","IMPRINT",FACE,{"disambiguationData":[TD([[makeQuery(id+"F0.imprint","IMPRINT",EDGE,{"derivedFrom":subQ0}),1.0]])]});}
            extrude(context, id + "F2", {"entities" : qUnion([Q0, Q1, Q2, Q3, Q4, Q5, Q6, Q7, Q8, Q9, Q10, Q11, Q12, Q13, Q14, Q15, Q16, Q17, Q18, Q19, Q20, Q21, Q22, Q23, Q24, Q25, Q26, Q27, Q28, Q29, Q30, Q31, Q32, Q33, Q34, Q35, Q36, Q37, Q38, Q39, Q40, Q41, Q42]), "operationType" : NewBodyOperationType.ADD, "depth" : 1 * mm, "offsetDistance" : 25 * mm});
        }
        {
            var Q0;
            Q0=makeQuery(id+"F1.opExtrude","SWEPT_EDGE",EDGE,{"disambiguationData":[OSD([sQuery(id+"F0.wireOp",EDGE,"E0.bottom"),sQuery(id+"F0.wireOp",EDGE,"E0.left")])]});
            var Q1;
            Q1=makeQuery(id+"F1.opExtrude","SWEPT_EDGE",EDGE,{"disambiguationData":[OSD([sQuery(id+"F0.wireOp",EDGE,"E0.bottom"),sQuery(id+"F0.wireOp",EDGE,"E0.right")])]});
            var Q2;
            Q2=makeQuery(id+"F1.opExtrude","SWEPT_EDGE",EDGE,{"disambiguationData":[OSD([sQuery(id+"F0.wireOp",EDGE,"E0.top"),sQuery(id+"F0.wireOp",EDGE,"E0.left")])]});
            var Q3;
            Q3=makeQuery(id+"F1.opExtrude","SWEPT_EDGE",EDGE,{"disambiguationData":[OSD([sQuery(id+"F0.wireOp",EDGE,"E0.top"),sQuery(id+"F0.wireOp",EDGE,"E4.bottom"),sQuery(id+"F0.wireOp",EDGE,"E4.left")])]});
            var Q4;
            Q4=makeQuery(id+"F1.opExtrude","SWEPT_EDGE",EDGE,{"disambiguationData":[OSD([sQuery(id+"F0.wireOp",EDGE,"E0.top"),sQuery(id+"F0.wireOp",EDGE,"E4.bottom"),sQuery(id+"F0.wireOp",EDGE,"E4.right")])]});
            var Q5;
            Q5=makeQuery(id+"F1.opExtrude","SWEPT_EDGE",EDGE,{"disambiguationData":[OSD([sQuery(id+"F0.wireOp",EDGE,"E0.top"),sQuery(id+"F0.wireOp",EDGE,"E0.right")])]});
            fillet(context, id + "F3", {"entities" : qUnion([Q0, Q1, Q2, Q3, Q4, Q5]), "radius" : 1 * mm, "tangentPropagation" : true, "allowEdgeOverflow" : false});
        }
        {
            var Q0;
            {var subQ69=sQuery(id+"F0.wireOp",EDGE,"E4.top");Q0=makeQuery(id+"F0.imprint","IMPRINT",FACE,{"disambiguationData":[TD([[makeQuery(id+"F0.imprint","IMPRINT",EDGE,{"derivedFrom":subQ69}),-1.0]])]});}
            extrude(context, id + "F4", {"entities" : qUnion([Q0]), "depth" : 33 * mm, "offsetDistance" : 25 * mm});
        }
        {
            var Q0;
            Q0=makeQuery(id+"F4.opExtrude","SWEPT_EDGE",EDGE,{"disambiguationData":[OSD([sQuery(id+"F0.wireOp",EDGE,"E2"),sQuery(id+"F0.wireOp",EDGE,"E28.top"),sQuery(id+"F0.wireOp",EDGE,"E28.left")])]});
            var Q1;
            Q1=makeQuery(id+"F4.opExtrude","SWEPT_EDGE",EDGE,{"disambiguationData":[OSD([sQuery(id+"F0.wireOp",EDGE,"E2"),sQuery(id+"F0.wireOp",EDGE,"E28.top"),sQuery(id+"F0.wireOp",EDGE,"E28.right")])]});
            var Q2;
            Q2=makeQuery(id+"F4.opExtrude","SWEPT_EDGE",EDGE,{"disambiguationData":[OSD([sQuery(id+"F0.wireOp",EDGE,"E2"),sQuery(id+"F0.wireOp",EDGE,"E23")])]});
            var Q3;
            Q3=makeQuery(id+"F4.opExtrude","SWEPT_EDGE",EDGE,{"disambiguationData":[OSD([sQuery(id+"F0.wireOp",EDGE,"E2"),sQuery(id+"F0.wireOp",EDGE,"E26")])]});
            var Q4;
            {var subQ0=sQuery(id+"F0.wireOp",EDGE,"E22.MirrorC");var subQ1=sQuery(id+"F0.wireOp",EDGE,"E2");Q4=makeQuery(id+"F4.opExtrude","SWEPT_EDGE",EDGE,{"disambiguationData":[OSD([subQ1,subQ0]),TDD([makeQuery(id+"F0.imprint","INTERSECT",VERTEX,{"disambiguationData":[OD(1.0)],"derivedFrom":[subQ1,subQ0]})])]});}
            var Q5;
            {var subQ0=sQuery(id+"F0.wireOp",EDGE,"E22.MirrorC");var subQ1=sQuery(id+"F0.wireOp",EDGE,"E2");Q5=makeQuery(id+"F4.opExtrude","SWEPT_EDGE",EDGE,{"disambiguationData":[OSD([subQ1,subQ0]),TDD([makeQuery(id+"F0.imprint","INTERSECT",VERTEX,{"disambiguationData":[OD(0.0)],"derivedFrom":[subQ1,subQ0]})])]});}
            var Q6;
            {var subQ0=sQuery(id+"F0.wireOp",EDGE,"E21.MirrorC");var subQ1=sQuery(id+"F0.wireOp",EDGE,"E2");Q6=makeQuery(id+"F4.opExtrude","SWEPT_EDGE",EDGE,{"disambiguationData":[OSD([subQ1,subQ0]),TDD([makeQuery(id+"F0.imprint","INTERSECT",VERTEX,{"disambiguationData":[OD(0.0)],"derivedFrom":[subQ1,subQ0]})])]});}
            var Q7;
            {var subQ0=sQuery(id+"F0.wireOp",EDGE,"E20.MirrorC");var subQ1=sQuery(id+"F0.wireOp",EDGE,"E2");Q7=makeQuery(id+"F4.opExtrude","SWEPT_EDGE",EDGE,{"disambiguationData":[OSD([subQ1,subQ0]),TDD([makeQuery(id+"F0.imprint","INTERSECT",VERTEX,{"disambiguationData":[OD(1.0)],"derivedFrom":[subQ1,subQ0]})])]});}
            var Q8;
            {var subQ0=sQuery(id+"F0.wireOp",EDGE,"E20.MirrorC");var subQ1=sQuery(id+"F0.wireOp",EDGE,"E2");Q8=makeQuery(id+"F4.opExtrude","SWEPT_EDGE",EDGE,{"disambiguationData":[OSD([subQ1,subQ0]),TDD([makeQuery(id+"F0.imprint","INTERSECT",VERTEX,{"disambiguationData":[OD(0.0)],"derivedFrom":[subQ1,subQ0]})])]});}
            var Q9;
            {var subQ0=sQuery(id+"F0.wireOp",EDGE,"E19.MirrorC");var subQ1=sQuery(id+"F0.wireOp",EDGE,"E2");Q9=makeQuery(id+"F4.opExtrude","SWEPT_EDGE",EDGE,{"disambiguationData":[OSD([subQ1,subQ0]),TDD([makeQuery(id+"F0.imprint","INTERSECT",VERTEX,{"disambiguationData":[OD(1.0)],"derivedFrom":[subQ1,subQ0]})])]});}
            var Q10;
            {var subQ0=sQuery(id+"F0.wireOp",EDGE,"E19.MirrorC");var subQ1=sQuery(id+"F0.wireOp",EDGE,"E2");Q10=makeQuery(id+"F4.opExtrude","SWEPT_EDGE",EDGE,{"disambiguationData":[OSD([subQ1,subQ0]),TDD([makeQuery(id+"F0.imprint","INTERSECT",VERTEX,{"disambiguationData":[OD(0.0)],"derivedFrom":[subQ1,subQ0]})])]});}
            var Q11;
            {var subQ0=sQuery(id+"F0.wireOp",EDGE,"E6");var subQ1=sQuery(id+"F0.wireOp",EDGE,"E2");Q11=makeQuery(id+"F4.opExtrude","SWEPT_EDGE",EDGE,{"disambiguationData":[OSD([subQ1,subQ0]),TDD([makeQuery(id+"F0.imprint","INTERSECT",VERTEX,{"disambiguationData":[OD(1.0)],"derivedFrom":[subQ1,subQ0]})])]});}
            var Q12;
            {var subQ0=sQuery(id+"F0.wireOp",EDGE,"E6");var subQ1=sQuery(id+"F0.wireOp",EDGE,"E2");Q12=makeQuery(id+"F4.opExtrude","SWEPT_EDGE",EDGE,{"disambiguationData":[OSD([subQ1,subQ0]),TDD([makeQuery(id+"F0.imprint","INTERSECT",VERTEX,{"disambiguationData":[OD(0.0)],"derivedFrom":[subQ1,subQ0]})])]});}
            var Q13;
            {var subQ0=sQuery(id+"F0.wireOp",EDGE,"E10");var subQ1=sQuery(id+"F0.wireOp",EDGE,"E2");Q13=makeQuery(id+"F4.opExtrude","SWEPT_EDGE",EDGE,{"disambiguationData":[OSD([subQ1,subQ0]),TDD([makeQuery(id+"F0.imprint","INTERSECT",VERTEX,{"disambiguationData":[OD(1.0)],"derivedFrom":[subQ1,subQ0]})])]});}
            var Q14;
            {var subQ0=sQuery(id+"F0.wireOp",EDGE,"E10");var subQ1=sQuery(id+"F0.wireOp",EDGE,"E2");Q14=makeQuery(id+"F4.opExtrude","SWEPT_EDGE",EDGE,{"disambiguationData":[OSD([subQ1,subQ0]),TDD([makeQuery(id+"F0.imprint","INTERSECT",VERTEX,{"disambiguationData":[OD(0.0)],"derivedFrom":[subQ1,subQ0]})])]});}
            var Q15;
            {var subQ0=sQuery(id+"F0.wireOp",EDGE,"E8");var subQ1=sQuery(id+"F0.wireOp",EDGE,"E2");Q15=makeQuery(id+"F4.opExtrude","SWEPT_EDGE",EDGE,{"disambiguationData":[OSD([subQ1,subQ0]),TDD([makeQuery(id+"F0.imprint","INTERSECT",VERTEX,{"disambiguationData":[OD(0.0)],"derivedFrom":[subQ1,subQ0]})])]});}
            var Q16;
            {var subQ0=sQuery(id+"F0.wireOp",EDGE,"E8");var subQ1=sQuery(id+"F0.wireOp",EDGE,"E2");Q16=makeQuery(id+"F4.opExtrude","SWEPT_EDGE",EDGE,{"disambiguationData":[OSD([subQ1,subQ0]),TDD([makeQuery(id+"F0.imprint","INTERSECT",VERTEX,{"disambiguationData":[OD(1.0)],"derivedFrom":[subQ1,subQ0]})])]});}
            var Q17;
            {var subQ0=sQuery(id+"F0.wireOp",EDGE,"E11");var subQ1=sQuery(id+"F0.wireOp",EDGE,"E2");Q17=makeQuery(id+"F4.opExtrude","SWEPT_EDGE",EDGE,{"disambiguationData":[OSD([subQ1,subQ0]),TDD([makeQuery(id+"F0.imprint","INTERSECT",VERTEX,{"disambiguationData":[OD(1.0)],"derivedFrom":[subQ1,subQ0]})])]});}
            var Q18;
            {var subQ0=sQuery(id+"F0.wireOp",EDGE,"E11");var subQ1=sQuery(id+"F0.wireOp",EDGE,"E2");Q18=makeQuery(id+"F4.opExtrude","SWEPT_EDGE",EDGE,{"disambiguationData":[OSD([subQ1,subQ0]),TDD([makeQuery(id+"F0.imprint","INTERSECT",VERTEX,{"disambiguationData":[OD(0.0)],"derivedFrom":[subQ1,subQ0]})])]});}
            var Q19;
            Q19=makeQuery(id+"F4.opExtrude","SWEPT_EDGE",EDGE,{"disambiguationData":[OSD([sQuery(id+"F0.wireOp",EDGE,"E2"),sQuery(id+"F0.wireOp",EDGE,"E18.left")])]});
            var Q20;
            Q20=makeQuery(id+"F4.opExtrude","SWEPT_EDGE",EDGE,{"disambiguationData":[OSD([sQuery(id+"F0.wireOp",EDGE,"E2"),sQuery(id+"F0.wireOp",EDGE,"E18.bottom")])]});
            var Q21;
            Q21=makeQuery(id+"F4.opExtrude","SWEPT_EDGE",EDGE,{"disambiguationData":[OSD([sQuery(id+"F0.wireOp",EDGE,"E2"),sQuery(id+"F0.wireOp",EDGE,"E32.MirrorCS"),sQuery(id+"F0.wireOp",EDGE,"E36.MirrorCS")])]});
            var Q22;
            Q22=makeQuery(id+"F4.opExtrude","SWEPT_EDGE",EDGE,{"disambiguationData":[OSD([sQuery(id+"F0.wireOp",EDGE,"E2"),sQuery(id+"F0.wireOp",EDGE,"E35.MirrorCS"),sQuery(id+"F0.wireOp",EDGE,"E36.MirrorCS")])]});
            var Q23;
            Q23=makeQuery(id+"F4.opExtrude","SWEPT_EDGE",EDGE,{"disambiguationData":[OSD([sQuery(id+"F0.wireOp",EDGE,"E2"),sQuery(id+"F0.wireOp",EDGE,"E97.2")])]});
            var Q24;
            Q24=makeQuery(id+"F4.opExtrude","SWEPT_EDGE",EDGE,{"disambiguationData":[OSD([sQuery(id+"F0.wireOp",EDGE,"E2"),sQuery(id+"F0.wireOp",EDGE,"E97.4")])]});
            var Q25;
            Q25=makeQuery(id+"F4.opExtrude","SWEPT_EDGE",EDGE,{"disambiguationData":[OSD([sQuery(id+"F0.wireOp",EDGE,"E4.top"),sQuery(id+"F0.wireOp",EDGE,"E97.0"),sQuery(id+"F0.wireOp",EDGE,"E97.1")])]});
            var Q26;
            Q26=makeQuery(id+"F4.opExtrude","SWEPT_EDGE",EDGE,{"disambiguationData":[OSD([sQuery(id+"F0.wireOp",EDGE,"E4.top"),sQuery(id+"F0.wireOp",EDGE,"E97.0"),sQuery(id+"F0.wireOp",EDGE,"E97.5")])]});
            var Q27;
            Q27=makeQuery(id+"F4.opExtrude","SWEPT_EDGE",EDGE,{"disambiguationData":[OSD([sQuery(id+"F0.wireOp",EDGE,"E27.top"),sQuery(id+"F0.wireOp",EDGE,"E28.left")])]});
            var Q28;
            Q28=makeQuery(id+"F4.opExtrude","SWEPT_EDGE",EDGE,{"disambiguationData":[OSD([sQuery(id+"F0.wireOp",EDGE,"E27.bottom"),sQuery(id+"F0.wireOp",EDGE,"E28.left")])]});
            var Q29;
            Q29=makeQuery(id+"F4.opExtrude","SWEPT_EDGE",EDGE,{"disambiguationData":[OSD([sQuery(id+"F0.wireOp",EDGE,"E27.bottom"),sQuery(id+"F0.wireOp",EDGE,"E27.left")])]});
            var Q30;
            Q30=makeQuery(id+"F4.opExtrude","SWEPT_EDGE",EDGE,{"disambiguationData":[OSD([sQuery(id+"F0.wireOp",EDGE,"E27.top"),sQuery(id+"F0.wireOp",EDGE,"E27.left")])]});
            var Q31;
            Q31=makeQuery(id+"F4.opExtrude","SWEPT_EDGE",EDGE,{"disambiguationData":[OSD([sQuery(id+"F0.wireOp",EDGE,"E27.top"),sQuery(id+"F0.wireOp",EDGE,"E28.right")])]});
            var Q32;
            Q32=makeQuery(id+"F4.opExtrude","SWEPT_EDGE",EDGE,{"disambiguationData":[OSD([sQuery(id+"F0.wireOp",EDGE,"E27.bottom"),sQuery(id+"F0.wireOp",EDGE,"E28.right")])]});
            var Q33;
            Q33=makeQuery(id+"F4.opExtrude","SWEPT_EDGE",EDGE,{"disambiguationData":[OSD([sQuery(id+"F0.wireOp",EDGE,"E27.top"),sQuery(id+"F0.wireOp",EDGE,"E27.right")])]});
            var Q34;
            Q34=makeQuery(id+"F4.opExtrude","SWEPT_EDGE",EDGE,{"disambiguationData":[OSD([sQuery(id+"F0.wireOp",EDGE,"E27.bottom"),sQuery(id+"F0.wireOp",EDGE,"E27.right")])]});
            var Q35;
            Q35=makeQuery(id+"F4.opExtrude","SWEPT_EDGE",EDGE,{"disambiguationData":[OSD([sQuery(id+"F0.wireOp",EDGE,"E23"),sQuery(id+"F0.wireOp",EDGE,"E24")])]});
            var Q36;
            Q36=makeQuery(id+"F4.opExtrude","SWEPT_EDGE",EDGE,{"disambiguationData":[OSD([sQuery(id+"F0.wireOp",EDGE,"E24"),sQuery(id+"F0.wireOp",EDGE,"E25")])]});
            var Q37;
            Q37=makeQuery(id+"F4.opExtrude","SWEPT_EDGE",EDGE,{"disambiguationData":[OSD([sQuery(id+"F0.wireOp",EDGE,"E25"),sQuery(id+"F0.wireOp",EDGE,"E26")])]});
            var Q38;
            Q38=makeQuery(id+"F4.opExtrude","SWEPT_EDGE",EDGE,{"disambiguationData":[OSD([sQuery(id+"F0.wireOp",EDGE,"E18.bottom"),sQuery(id+"F0.wireOp",EDGE,"E18.right")])]});
            var Q39;
            Q39=makeQuery(id+"F4.opExtrude","SWEPT_EDGE",EDGE,{"disambiguationData":[OSD([sQuery(id+"F0.wireOp",EDGE,"E18.top"),sQuery(id+"F0.wireOp",EDGE,"E18.left")])]});
            var Q40;
            Q40=makeQuery(id+"F4.opExtrude","SWEPT_EDGE",EDGE,{"disambiguationData":[OSD([sQuery(id+"F0.wireOp",EDGE,"E18.top"),sQuery(id+"F0.wireOp",EDGE,"E18.right")])]});
            var Q41;
            Q41=makeQuery(id+"F4.opExtrude","SWEPT_EDGE",EDGE,{"disambiguationData":[OSD([sQuery(id+"F0.wireOp",EDGE,"E12"),sQuery(id+"F0.wireOp",EDGE,"E13")])]});
            var Q42;
            Q42=makeQuery(id+"F4.opExtrude","SWEPT_EDGE",EDGE,{"disambiguationData":[OSD([sQuery(id+"F0.wireOp",EDGE,"E12"),sQuery(id+"F0.wireOp",EDGE,"E14")])]});
            var Q43;
            Q43=makeQuery(id+"F4.opExtrude","SWEPT_EDGE",EDGE,{"disambiguationData":[OSD([sQuery(id+"F0.wireOp",EDGE,"E33.MirrorCS"),sQuery(id+"F0.wireOp",EDGE,"E37.MirrorCS")])]});
            var Q44;
            Q44=makeQuery(id+"F4.opExtrude","SWEPT_EDGE",EDGE,{"disambiguationData":[OSD([sQuery(id+"F0.wireOp",EDGE,"E34.MirrorCS"),sQuery(id+"F0.wireOp",EDGE,"E37.MirrorCS")])]});
            var Q45;
            Q45=makeQuery(id+"F4.opExtrude","SWEPT_EDGE",EDGE,{"disambiguationData":[OSD([sQuery(id+"F0.wireOp",EDGE,"E35.MirrorCS"),sQuery(id+"F0.wireOp",EDGE,"E37.MirrorCS")])]});
            var Q46;
            Q46=makeQuery(id+"F4.opExtrude","SWEPT_EDGE",EDGE,{"disambiguationData":[OSD([sQuery(id+"F0.wireOp",EDGE,"E32.MirrorCS"),sQuery(id+"F0.wireOp",EDGE,"E37.MirrorCS")])]});
            var Q47;
            Q47=makeQuery(id+"F4.opExtrude","SWEPT_EDGE",EDGE,{"disambiguationData":[OSD([sQuery(id+"F0.wireOp",EDGE,"E31.MirrorCS"),sQuery(id+"F0.wireOp",EDGE,"E33.MirrorCS")])]});
            var Q48;
            Q48=makeQuery(id+"F4.opExtrude","SWEPT_EDGE",EDGE,{"disambiguationData":[OSD([sQuery(id+"F0.wireOp",EDGE,"E31.MirrorCS"),sQuery(id+"F0.wireOp",EDGE,"E32.MirrorCS")])]});
            var Q49;
            Q49=makeQuery(id+"F4.opExtrude","SWEPT_EDGE",EDGE,{"disambiguationData":[OSD([sQuery(id+"F0.wireOp",EDGE,"E30.MirrorCS"),sQuery(id+"F0.wireOp",EDGE,"E32.MirrorCS")])]});
            var Q50;
            Q50=makeQuery(id+"F4.opExtrude","SWEPT_EDGE",EDGE,{"disambiguationData":[OSD([sQuery(id+"F0.wireOp",EDGE,"E30.MirrorCS"),sQuery(id+"F0.wireOp",EDGE,"E35.MirrorCS")])]});
            var Q51;
            Q51=makeQuery(id+"F4.opExtrude","SWEPT_EDGE",EDGE,{"disambiguationData":[OSD([sQuery(id+"F0.wireOp",EDGE,"E31.MirrorCS"),sQuery(id+"F0.wireOp",EDGE,"E35.MirrorCS")])]});
            var Q52;
            Q52=makeQuery(id+"F4.opExtrude","SWEPT_EDGE",EDGE,{"disambiguationData":[OSD([sQuery(id+"F0.wireOp",EDGE,"E31.MirrorCS"),sQuery(id+"F0.wireOp",EDGE,"E34.MirrorCS")])]});
            var Q53;
            {var subQ0=sQuery(id+"F0.wireOp",EDGE,"E21.MirrorC");var subQ1=sQuery(id+"F0.wireOp",EDGE,"E2");Q53=makeQuery(id+"F4.opExtrude","SWEPT_EDGE",EDGE,{"disambiguationData":[OSD([subQ1,subQ0]),TDD([makeQuery(id+"F0.imprint","INTERSECT",VERTEX,{"disambiguationData":[OD(1.0)],"derivedFrom":[subQ1,subQ0]})])]});}
            fillet(context, id + "F5", {"entities" : qUnion([Q0, Q1, Q2, Q3, Q4, Q5, Q6, Q7, Q8, Q9, Q10, Q11, Q12, Q13, Q14, Q15, Q16, Q17, Q18, Q19, Q20, Q21, Q22, Q23, Q24, Q25, Q26, Q27, Q28, Q29, Q30, Q31, Q32, Q33, Q34, Q35, Q36, Q37, Q38, Q39, Q40, Q41, Q42, Q43, Q44, Q45, Q46, Q47, Q48, Q49, Q50, Q51, Q52, Q53]), "radius" : 1 * mm, "tangentPropagation" : true, "allowEdgeOverflow" : false});
        }
        {
            var Q0;
            Q0=makeQuery(id+"F4.opExtrude","SWEPT_EDGE",EDGE,{"disambiguationData":[OSD([sQuery(id+"F0.wireOp",EDGE,"E4.top"),sQuery(id+"F0.wireOp",EDGE,"E4.right")])]});
            var Q1;
            Q1=makeQuery(id+"F4.opExtrude","SWEPT_EDGE",EDGE,{"disambiguationData":[OSD([sQuery(id+"F0.wireOp",EDGE,"E4.top"),sQuery(id+"F0.wireOp",EDGE,"E4.left")])]});
            var Q2;
            Q2=makeQuery(id+"F4.opExtrude","SWEPT_EDGE",EDGE,{"disambiguationData":[OSD([sQuery(id+"F0.wireOp",EDGE,"E2"),sQuery(id+"F0.wireOp",EDGE,"E14")])]});
            var Q3;
            Q3=makeQuery(id+"F2.opExtrude","SWEPT_EDGE",EDGE,{"disambiguationData":[OSD([sQuery(id+"F0.wireOp",EDGE,"E2"),sQuery(id+"F0.wireOp",EDGE,"E14"),sQuery(id+"F0.wireOp",EDGE,"E106")])]});
            var Q4;
            Q4=makeQuery(id+"F2.opExtrude","SWEPT_EDGE",EDGE,{"disambiguationData":[OSD([sQuery(id+"F0.wireOp",EDGE,"E2"),sQuery(id+"F0.wireOp",EDGE,"E13"),sQuery(id+"F0.wireOp",EDGE,"E106")])]});
            var Q5;
            Q5=makeQuery(id+"F4.opExtrude","SWEPT_EDGE",EDGE,{"disambiguationData":[OSD([sQuery(id+"F0.wireOp",EDGE,"E2"),sQuery(id+"F0.wireOp",EDGE,"E13"),sQuery(id+"F0.wireOp",EDGE,"E106")])]});
            fillet(context, id + "F6", {"entities" : qUnion([Q0, Q1, Q2, Q3, Q4, Q5]), "radius" : 3 * mm, "tangentPropagation" : true, "allowEdgeOverflow" : false});
        }
        {
            var Q0;
            Q0=makeQuery(id+"F0.imprint","IMPRINT",FACE,{"disambiguationData":[TD([[makeQuery(id+"F0.imprint","IMPRINT",EDGE,{"derivedFrom":sQuery(id+"F0.wireOp",EDGE,"E90.bottom")}),-1.0]])]});
            var Q1;
            Q1=makeQuery(id+"F0.imprint","IMPRINT",FACE,{"disambiguationData":[TD([[makeQuery(id+"F0.imprint","IMPRINT",EDGE,{"derivedFrom":sQuery(id+"F0.wireOp",EDGE,"E79.bottom")}),1.0]])]});
            var Q2;
            Q2=makeQuery(id+"F0.imprint","IMPRINT",FACE,{"disambiguationData":[TD([[makeQuery(id+"F0.imprint","IMPRINT",EDGE,{"derivedFrom":sQuery(id+"F0.wireOp",EDGE,"E77.bottom")}),1.0]])]});
            var Q3;
            Q3=makeQuery(id+"F0.imprint","IMPRINT",FACE,{"disambiguationData":[TD([[makeQuery(id+"F0.imprint","IMPRINT",EDGE,{"derivedFrom":sQuery(id+"F0.wireOp",EDGE,"E88.bottom")}),-1.0]])]});
            var Q4;
            Q4=makeQuery(id+"F0.imprint","IMPRINT",FACE,{"disambiguationData":[TD([[makeQuery(id+"F0.imprint","IMPRINT",EDGE,{"derivedFrom":sQuery(id+"F0.wireOp",EDGE,"E80.MirrorCS")}),-1.0]])]});
            var Q5;
            Q5=makeQuery(id+"F0.imprint","IMPRINT",FACE,{"disambiguationData":[TD([[makeQuery(id+"F0.imprint","IMPRINT",EDGE,{"derivedFrom":sQuery(id+"F0.wireOp",EDGE,"E84.MirrorCS")}),-1.0]])]});
            var Q6;
            Q6=makeQuery(id+"F0.imprint","IMPRINT",FACE,{"disambiguationData":[TD([[makeQuery(id+"F0.imprint","IMPRINT",EDGE,{"derivedFrom":sQuery(id+"F0.wireOp",EDGE,"E91.MirrorCS")}),1.0]])]});
            extrude(context, id + "F7", {"entities" : qUnion([Q0, Q1, Q2, Q3, Q4, Q5, Q6]), "operationType" : NewBodyOperationType.ADD, "depth" : 5 * mm, "offsetDistance" : 25 * mm});
        }
    });
